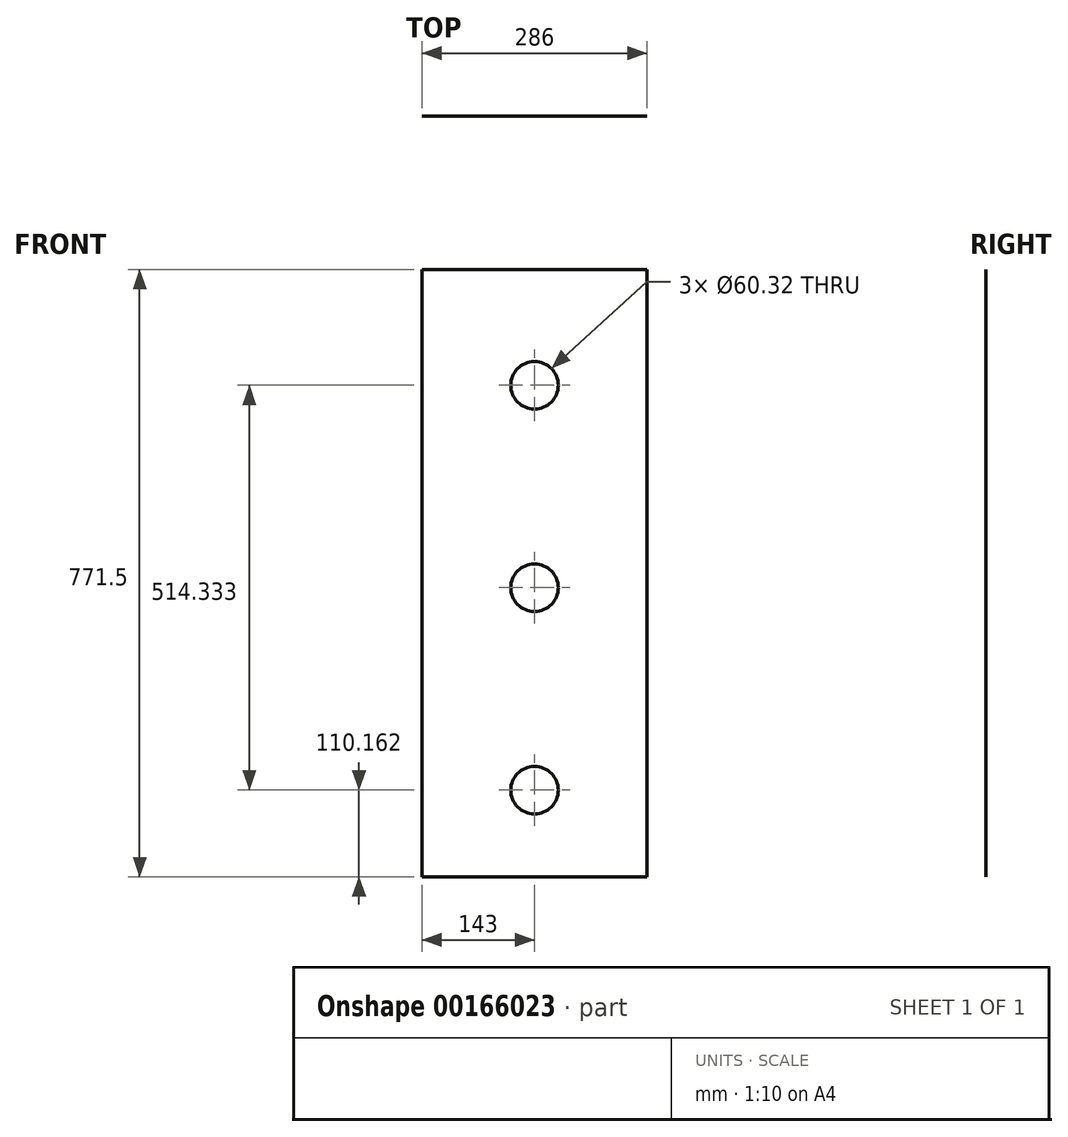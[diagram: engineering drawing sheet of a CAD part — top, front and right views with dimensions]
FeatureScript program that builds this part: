
annotation { "Feature Type Name" : "Feature", "Feature Type Description" : "" }
export const myFeature = defineFeature(function(context is Context, id is Id, definition is map)
    precondition{}
    {
        {
            var Q0;
            Q0=qCreatedBy(makeId("Front.planeOp"),FACE);
            var sketch = newSketch(context, id + "F0", { "sketchPlane" : qUnion([Q0])});
            skLineSegment(sketch, "E0.bottom", {"start": v(0, 0) * mm, "end": v(286, 0) * mm});
            skLineSegment(sketch, "E0.top", {"start": v(0, 771.5) * mm, "end": v(286, 771.5) * mm});
            skLineSegment(sketch, "E0.left", {"start": v(0, 0) * mm, "end": v(0, 771.5) * mm});
            skLineSegment(sketch, "E0.right", {"start": v(286, 0) * mm, "end": v(286, 771.5) * mm});
            skLineSegment(sketch, "E1", {"start": v(10, 771.5) * mm, "end": v(10, 0) * mm, "construction": true});
            skLineSegment(sketch, "E2", {"start": v(276, 771.5) * mm, "end": v(276, 0) * mm, "construction": true});
            skLineSegment(sketch, "E3", {"start": v(0, 514.33) * mm, "end": v(286, 514.33) * mm, "construction": true});
            skLineSegment(sketch, "E4", {"start": v(0, 257.17) * mm, "end": v(286, 257.17) * mm, "construction": true});
            skLineSegment(sketch, "E5", {"start": v(286, 257.17) * mm, "end": v(0, 0) * mm, "construction": true});
            skLineSegment(sketch, "E6", {"start": v(0, 257.17) * mm, "end": v(286, 514.33) * mm, "construction": true});
            skLineSegment(sketch, "E7", {"start": v(0, 514.33) * mm, "end": v(286, 771.5) * mm, "construction": true});
            skLineSegment(sketch, "E8", {"start": v(143, 771.5) * mm, "end": v(143, 0) * mm, "construction": true});
            skCircle(sketch, "E9", {"center": v(143, 110.16) * mm, "radius": 30.16 * mm});
            skCircle(sketch, "E10", {"center": v(143, 367.33) * mm, "radius": 30.16 * mm});
            skCircle(sketch, "E11", {"center": v(143, 624.5) * mm, "radius": 30.16 * mm});
            skSolve(sketch);
        }
        {
            var Q0;
            Q0=makeQuery(id+"F0.imprint","IMPRINT",FACE,{"disambiguationData":[TD([[makeQuery(id+"F0.imprint","IMPRINT",EDGE,{"derivedFrom":sQuery(id+"F0.wireOp",EDGE,"E0.bottom")}),1.0]])]});
            extrude(context, id + "F1", {"entities" : qUnion([Q0]), "depth" : 1 / 203.2 * mm});
        }
    });
